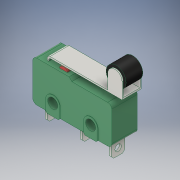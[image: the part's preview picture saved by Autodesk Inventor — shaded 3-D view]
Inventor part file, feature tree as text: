
AUTODESK INVENTOR PART (.ipt)
format: ipt  version: 2019 (Build 230136000, 136)  size: 297,472 bytes
history: native  units: mm
features: sketch x9, extrude x8, other x1, hole x1, chamfer x1
ambient origin geometry x8: Origin, YZ Plane, XZ Plane, XY Plane, X Axis, Y Axis, Z Axis, Center Point
bodies: Body1 (feature_tree)
feature tree (20):
  other  "Твердое тело1"
  extrude  "Выдавливание1"  Depth=19.8mm
  extrude  "Выдавливание2"  Depth=9.5mm
  extrude  "Выдавливание3"  Depth=10.0mm
  hole  "Отверстие1"  [1 undecoded]
  extrude  "Выдавливание4"  Depth=10.2mm
  extrude  "Выдавливание5"  Depth=1.0mm
  extrude  "Выдавливание6"  Depth=6.4mm TaperAngle=0.0deg
  extrude  "Выдавливание7"  Depth=0.5mm
  chamfer  "Фаска1"  Distance=8.8mm
  extrude  "Выдавливание8"  Depth=7.3mm
  sketch  "Эскиз2"
  sketch  "Эскиз3"
  sketch  "Эскиз4"
  sketch  "Эскиз6"
  sketch  "Эскиз7"
  sketch  "Эскиз8"
  sketch  "Эскиз9"
  sketch  "Эскиз10"
  sketch  "Эскиз11"
note: 1 required parameter value undecoded (feature->parameter linkage not recoverable at this tier; creation-order binding heuristic only, values carry confidence <= 0.55)
